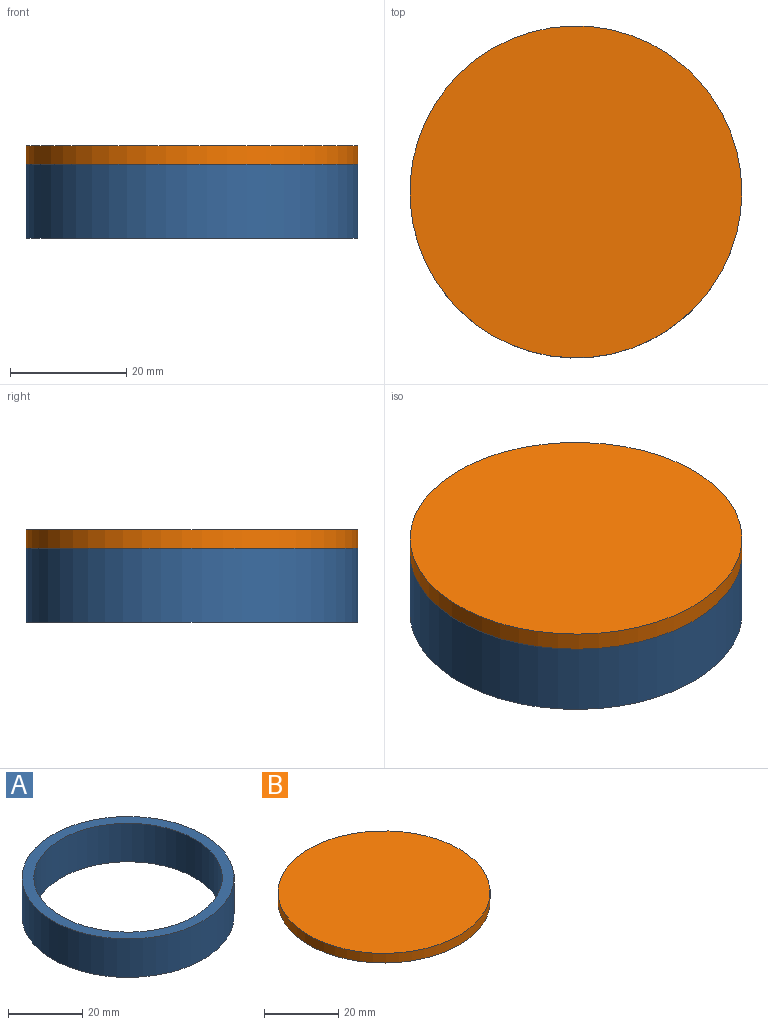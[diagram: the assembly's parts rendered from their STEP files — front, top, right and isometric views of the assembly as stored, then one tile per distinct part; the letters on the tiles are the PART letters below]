
ASSEMBLY  parts=2 mates=1
PART A: 4 faces, bbox 57.2x57.2x12.7 mm
  f0: cylinder r=25.4mm len=50.8mm, axis (0,0,-1), area 2026.8mm2, adj f2,f3
  f1: cylinder r=28.57mm len=57.15mm, axis (0,0,-1), area 2280.2mm2, adj f2,f3
  f2: plane 57.15x57.15mm, normal (0,0,1), area 538.4mm2, adj f0,f1
  f3: plane 57.15x57.15mm, normal (0,0,-1), area 538.4mm2, adj f0,f1
PART B: 3 faces, bbox 57.2x57.2x3.2 mm
  f0: cylinder r=28.57mm len=57.15mm, axis (0,0,-1), area 570mm2, adj f1,f2
  f1: plane 57.15x57.15mm, normal (0,0,1), area 2565.2mm2, adj f0
  f2: plane 57.15x57.15mm, normal (0,0,-1), area 2565.2mm2, adj f0
PLACE A t=(-6.54,3.75,-1.42)mm
PLACE B t=(-6.54,3.75,11.28)mm
MATE fastened B.f0 <-> A.f1  axis (0,0,-1) through (-6.54,3.75,11.28)mm
